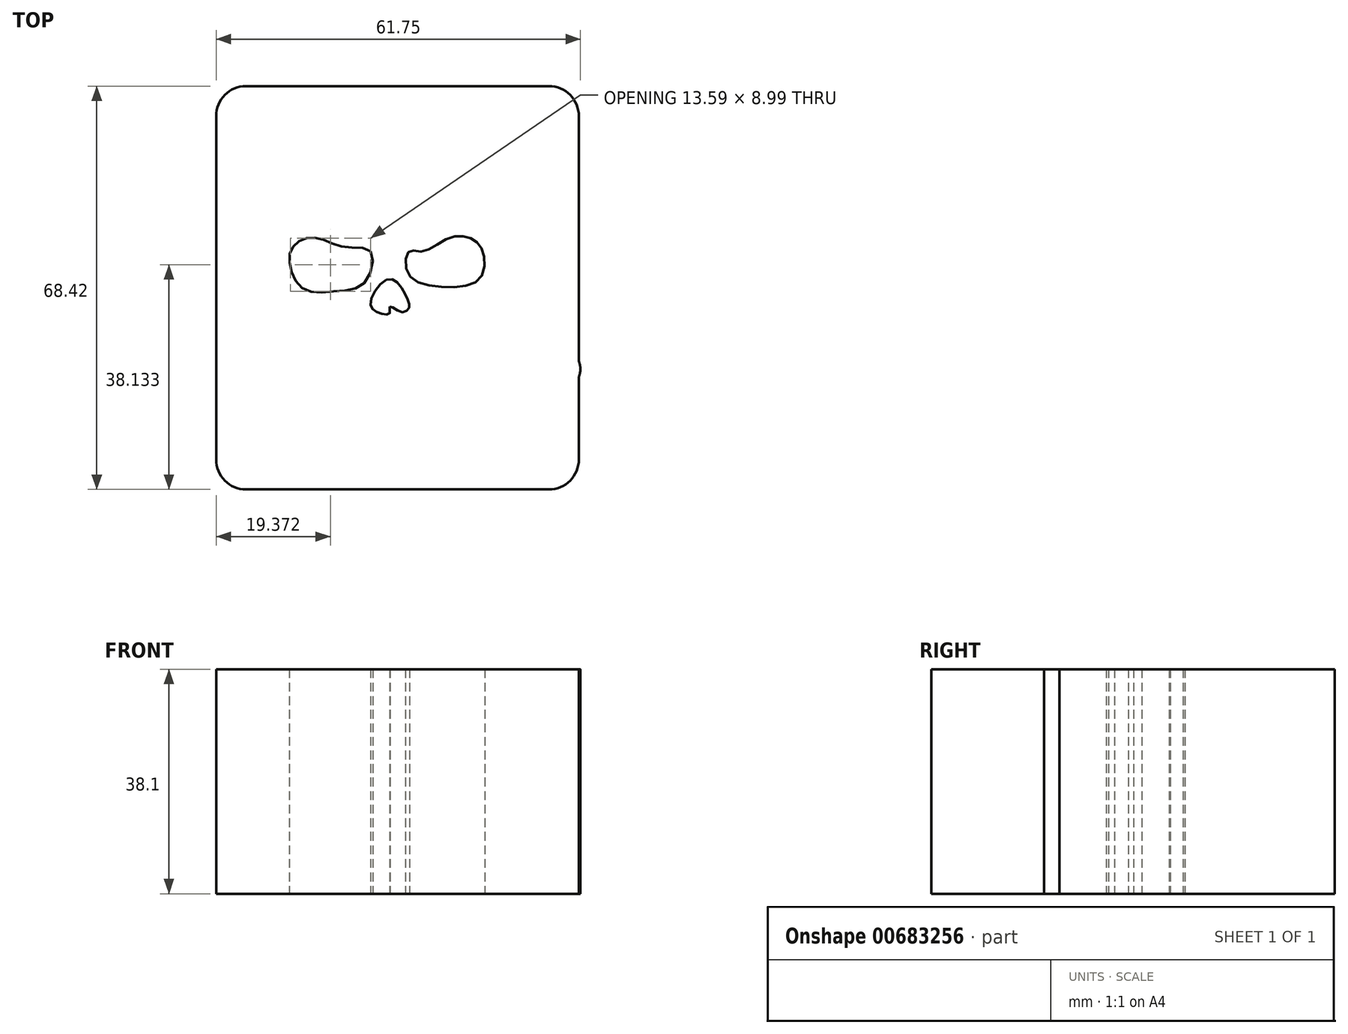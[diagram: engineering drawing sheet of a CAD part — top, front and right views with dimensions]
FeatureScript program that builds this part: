
annotation { "Feature Type Name" : "Feature", "Feature Type Description" : "" }
export const myFeature = defineFeature(function(context is Context, id is Id, definition is map)
    precondition{}
    {
        {
            var Q0;
            Q0=qCreatedBy(makeId("Top.planeOp"),FACE);
            var sketch = newSketch(context, id + "F0", { "sketchPlane" : qUnion([Q0])});
            skFitSpline(sketch, "E0", {"points": [v(-3.27, 14.3) * mm, v(-7.57, 15.05) * mm, v(-11.5, 16.36) * mm, v(-14.67, 16.36) * mm, v(-16.73, 14.49) * mm, v(-16.73, 11.12) * mm, v(-14.3, 7.76) * mm, v(-8.88, 7.57) * mm, v(-4.2, 9.07) * mm, v(-3.27, 14.3) * mm]});
            skFitSpline(sketch, "E1", {"points": [v(13.74, 16.54) * mm, v(10, 16.54) * mm, v(5.51, 14.3) * mm, v(3.27, 14.3) * mm, v(3.08, 10.56) * mm, v(8.7, 8.32) * mm, v(15.24, 9.63) * mm, v(15.8, 14.3) * mm, v(13.74, 16.54) * mm]});
            skFitSpline(sketch, "E2", {"points": [v(0, 4.95) * mm, v(0, 3.83) * mm, v(-1.78, 3.83) * mm, v(-3.27, 5.51) * mm, v(0, 9.63) * mm, v(2.71, 6.82) * mm, v(3.27, 4.77) * mm, v(1.96, 4.02) * mm, v(0, 4.95) * mm]});
            skFitSpline(sketch, "E3", {"points": [v(10.38, 0) * mm, v(12.24, -2.52) * mm, v(12.24, -4.58) * mm, v(15.8, -3.46) * mm, v(19.9, -2.15) * mm, v(23.65, 0) * mm, v(24.77, 1.59) * mm, v(26.83, 1.78) * mm, v(27.76, -1.4) * mm, v(31.5, -3.46) * mm, v(31.5, -7.76) * mm, v(25.14, -7.94) * mm, v(22.15, -7.2) * mm, v(15.8, -7.94) * mm, v(12.24, -9.63) * mm, v(19.9, -11.5) * mm, v(22.53, -9.25) * mm, v(25.52, -10.19) * mm, v(25.33, -14.3) * mm, v(26.64, -15.98) * mm, v(26.26, -20.1) * mm, v(21.97, -20.66) * mm, v(18.41, -16.92) * mm, v(4.95, -13.37) * mm, v(1.96, -12.62) * mm, v(-6.82, -14.49) * mm, v(-11.12, -15.24) * mm, v(-13.74, -16.73) * mm, v(-15.6, -20.1) * mm, v(-19.16, -21.03) * mm, v(-20.66, -18.79) * mm, v(-24.4, -17.48) * mm, v(-25.7, -14.3) * mm, v(-23.09, -11.87) * mm, v(-16.92, -12.43) * mm, v(-11.5, -10) * mm, v(-18.79, -8.5) * mm, v(-23.09, -10.19) * mm, v(-25.9, -9.63) * mm, v(-26.45, -7.2) * mm, v(-28.88, -3.83) * mm, v(-27.57, -1.59) * mm, v(-24.77, 0) * mm, v(-20.47, -2.52) * mm, v(-10.56, -4.58) * mm, v(-11.3, -2.9) * mm, v(-9.07, 0) * mm, v(-13.37, 0) * mm, v(-18.6, 0) * mm, v(-19.35, 2.34) * mm, v(-18.23, 4.77) * mm, v(-20.66, 9.63) * mm, v(-21.6, 14.3) * mm, v(-20.47, 17.3) * mm, v(-20.28, 24.58) * mm, v(-15.24, 35.61) * mm, v(0, 41.97) * mm, v(13, 38.23) * mm, v(19.72, 30.2) * mm, v(21.4, 19.35) * mm, v(23.09, 14.3) * mm, v(19.16, 6.82) * mm, v(20.47, 4.77) * mm, v(18.23, 0) * mm, v(10.38, 0) * mm]});
            skLineSegment(sketch, "E4.bottom", {"start": v(-24.36, -26.08) * mm, "end": v(26.98, -26.08) * mm});
            skLineSegment(sketch, "E4.top", {"start": v(-24.36, 42.34) * mm, "end": v(26.98, 42.34) * mm});
            skLineSegment(sketch, "E4.left", {"start": v(-29.44, -21) * mm, "end": v(-29.44, 37.26) * mm});
            skLineSegment(sketch, "E4.right", {"start": v(32.06, -21) * mm, "end": v(32.06, 37.26) * mm});
            skPoint(sketch, "E5.visualSharp", {"position": v(32.06, 42.34) * mm});
            skArc(sketch, "E5.filletArc", {"start": v(32.06, 37.26) * mm, "mid": v(30.57, 40.85) * mm, "end": v(26.98, 42.34) * mm});
            skPoint(sketch, "E6.visualSharp", {"position": v(-29.44, 42.34) * mm});
            skArc(sketch, "E6.filletArc", {"start": v(-24.36, 42.34) * mm, "mid": v(-27.96, 40.85) * mm, "end": v(-29.44, 37.26) * mm});
            skPoint(sketch, "E7.visualSharp", {"position": v(-29.44, -26.08) * mm});
            skArc(sketch, "E7.filletArc", {"start": v(-29.44, -21) * mm, "mid": v(-27.96, -24.6) * mm, "end": v(-24.36, -26.08) * mm});
            skPoint(sketch, "E8.visualSharp", {"position": v(32.06, -26.08) * mm});
            skArc(sketch, "E8.filletArc", {"start": v(26.98, -26.08) * mm, "mid": v(30.57, -24.6) * mm, "end": v(32.06, -21) * mm});
            skSolve(sketch);
        }
        {
            var Q0;
            Q0 = qSketchRegion(id + "F0", true);
            extrude(context, id + "F1", {"entities" : qUnion([Q0]), "depth" : 12.7 * mm, "offsetDistance" : 25.4 * mm});
        }
        {
            var Q0;
            Q0=makeQuery(id+"F1.opExtrude","CAP_FACE",FACE,{"disambiguationData":[OSD([sQuery(id+"F0.wireOp",EDGE,"E0"),sQuery(id+"F0.wireOp",EDGE,"E1"),sQuery(id+"F0.wireOp",EDGE,"E2"),sQuery(id+"F0.wireOp",EDGE,"E3"),sQuery(id+"F0.wireOp",EDGE,"E4.bottom"),sQuery(id+"F0.wireOp",EDGE,"E4.top"),sQuery(id+"F0.wireOp",EDGE,"E4.left"),sQuery(id+"F0.wireOp",EDGE,"E4.right"),sQuery(id+"F0.wireOp",EDGE,"E5.filletArc"),sQuery(id+"F0.wireOp",EDGE,"E6.filletArc"),sQuery(id+"F0.wireOp",EDGE,"E7.filletArc"),sQuery(id+"F0.wireOp",EDGE,"E8.filletArc")])],"isStart":true});
            extrude(context, id + "F2", {"entities" : qUnion([Q0]), "operationType" : NewBodyOperationType.ADD, "depth" : 25.4 * mm, "offsetDistance" : 25.4 * mm});
        }
    });
